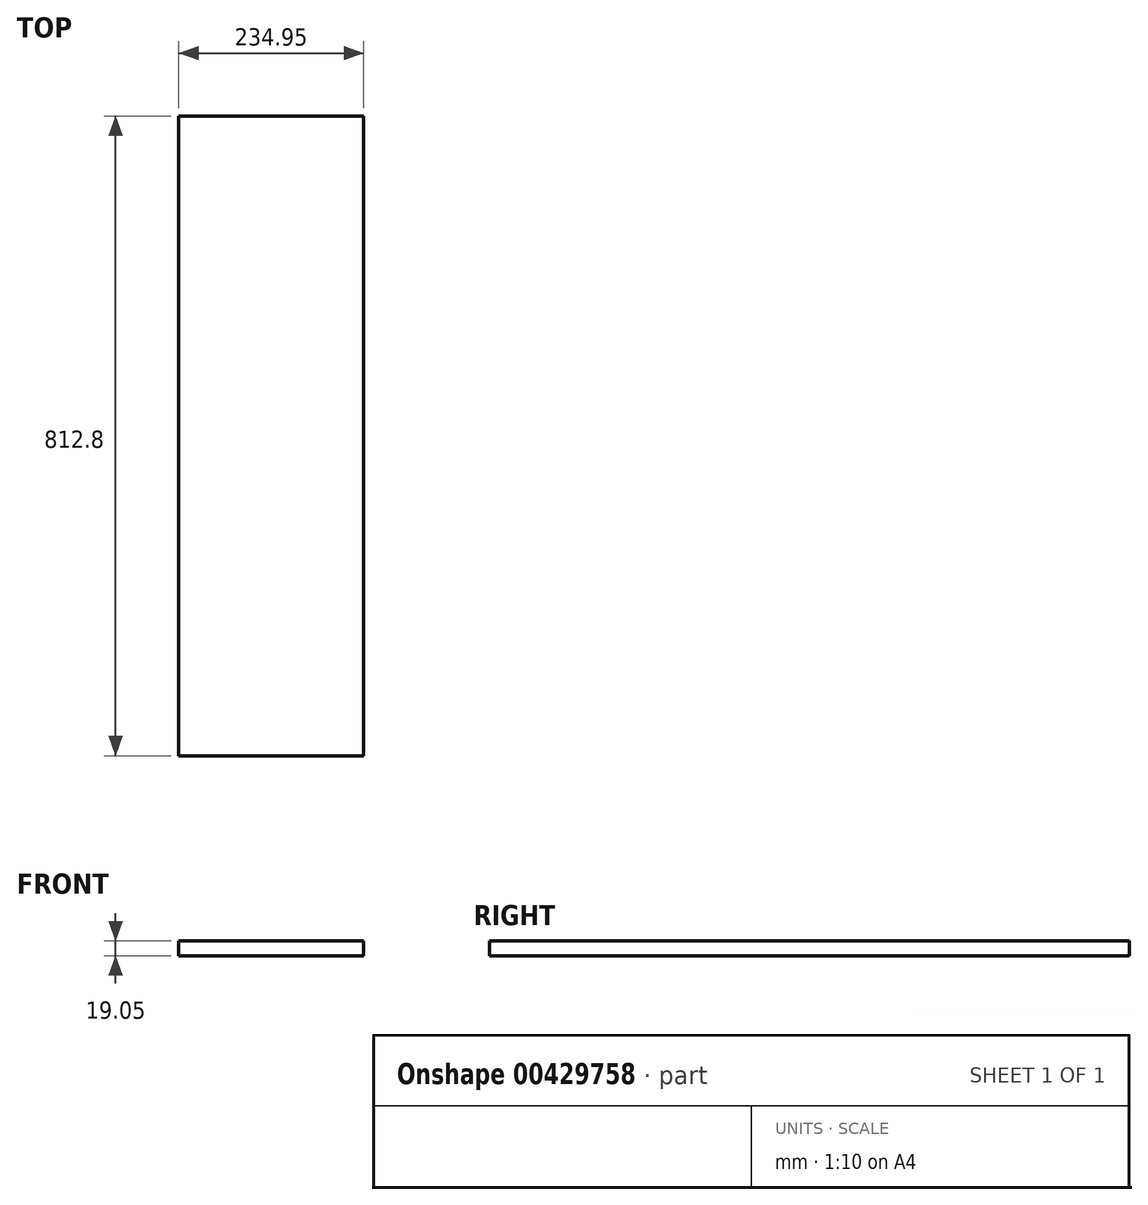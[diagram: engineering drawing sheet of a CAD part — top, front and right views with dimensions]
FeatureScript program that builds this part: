
annotation { "Feature Type Name" : "Feature", "Feature Type Description" : "" }
export const myFeature = defineFeature(function(context is Context, id is Id, definition is map)
    precondition{}
    {
        {
            var Q0;
            Q0=qCreatedBy(makeId("Top.planeOp"),FACE);
            var sketch = newSketch(context, id + "F0", { "sketchPlane" : qUnion([Q0])});
            skLineSegment(sketch, "E0", {"start": v(0, 0) * mm, "end": v(-234.95, 0) * mm});
            skLineSegment(sketch, "E1", {"start": v(-234.95, 0) * mm, "end": v(-234.95, -812.8) * mm});
            skLineSegment(sketch, "E2", {"start": v(-234.95, -812.8) * mm, "end": v(0, -812.8) * mm});
            skLineSegment(sketch, "E3", {"start": v(0, -812.8) * mm, "end": v(0, 0) * mm});
            skSolve(sketch);
        }
        {
            var Q0;
            Q0 = qSketchRegion(id + "F0", true);
            extrude(context, id + "F1", {"entities" : qUnion([Q0]), "depth" : 19.05 * mm});
        }
    });
